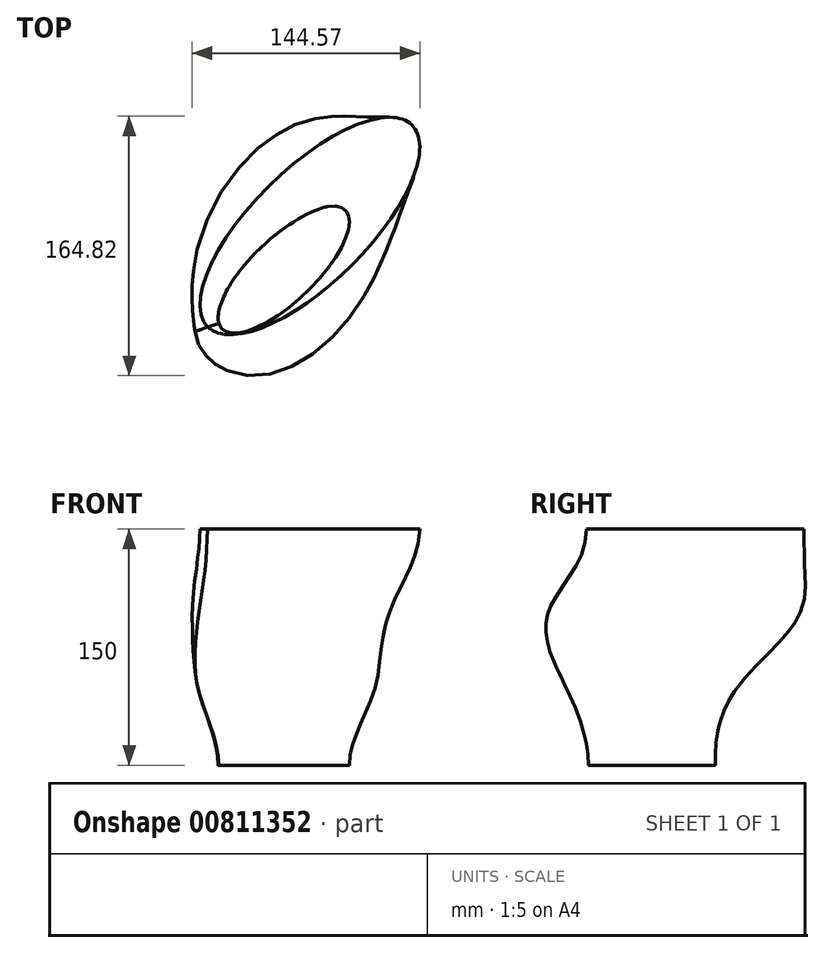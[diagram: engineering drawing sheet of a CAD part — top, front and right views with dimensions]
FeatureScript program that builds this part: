
annotation { "Feature Type Name" : "Feature", "Feature Type Description" : "" }
export const myFeature = defineFeature(function(context is Context, id is Id, definition is map)
    precondition{}
    {
        {
            var Q0;
            Q0=qCreatedBy(makeId("Top.planeOp"),FACE);
            var sketch = newSketch(context, id + "F0", { "sketchPlane" : qUnion([Q0])});
            skEllipse(sketch, "E0", {"center": v(36.85, 27.7) * mm, "majorRadius": 91.27 * mm, "minorRadius": 36.4 * mm, "majorAxis": v(-0.71, -0.7)});
            skSolve(sketch);
        }
        {
            var Q0;
            Q0=qCreatedBy(makeId("Top.planeOp"),FACE);
            cPlane(context, id + "F1", {"entities" : qUnion([Q0]), "cplaneType" : CPlaneType.OFFSET, "offset" : 50 * mm, "oppositeDirection" : true, "width" : 150 * mm, "height" : 150 * mm});
        }
        {
            var Q0;
            Q0=qCreatedBy(id+"F1.planeOp",FACE);
            var sketch = newSketch(context, id + "F2", { "sketchPlane" : qUnion([Q0])});
            skEllipse(sketch, "E1", {"center": v(25.4, 15.4) * mm, "majorRadius": 85.47 * mm, "minorRadius": 55.7 * mm, "majorAxis": v(0.46, 0.89)});
            skSolve(sketch);
        }
        {
            var Q0;
            Q0=qCreatedBy(id+"F1.planeOp",FACE);
            cPlane(context, id + "F3", {"entities" : qUnion([Q0]), "cplaneType" : CPlaneType.OFFSET, "offset" : 50 * mm, "oppositeDirection" : true, "width" : 150 * mm, "height" : 150 * mm});
        }
        {
            var Q0;
            Q0=qCreatedBy(id+"F3.planeOp",FACE);
            var sketch = newSketch(context, id + "F4", { "sketchPlane" : qUnion([Q0])});
            skEllipse(sketch, "E2", {"center": v(22.04, 0) * mm, "majorRadius": 71.84 * mm, "minorRadius": 31.93 * mm, "majorAxis": v(-0.72, -0.69)});
            skSolve(sketch);
        }
        {
            var Q0;
            Q0=qCreatedBy(id+"F3.planeOp",FACE);
            cPlane(context, id + "F5", {"entities" : qUnion([Q0]), "cplaneType" : CPlaneType.OFFSET, "offset" : 50 * mm, "oppositeDirection" : true, "width" : 150 * mm, "height" : 150 * mm});
        }
        {
            var Q0;
            Q0=qCreatedBy(id+"F5.planeOp",FACE);
            var sketch = newSketch(context, id + "F6", { "sketchPlane" : qUnion([Q0])});
            skEllipse(sketch, "E3", {"center": v(20.29, 0) * mm, "majorRadius": 54.33 * mm, "minorRadius": 20.27 * mm, "majorAxis": v(0.72, 0.7)});
            skSolve(sketch);
        }
        {
            var Q0;
            Q0 = qSketchRegion(id + "F0", true);
            var Q1;
            Q1 = qSketchRegion(id + "F2", true);
            var Q2;
            Q2 = qSketchRegion(id + "F4", true);
            var Q3;
            Q3 = qSketchRegion(id + "F6", true);
            var Q4;
            Q4=sQuery(id+"F0.wireOp",EDGE,"E0");
            var Q5;
            Q5=sQuery(id+"F2.wireOp",EDGE,"E1");
            var Q6;
            Q6=sQuery(id+"F4.wireOp",EDGE,"E2");
            var Q7;
            Q7=sQuery(id+"F6.wireOp",EDGE,"E3");
            loft(context, id + "F7", {"bodyType" : ToolBodyType.SURFACE, "startCondition" : LoftEndDerivativeType.NORMAL_TO_PROFILE, "startMagnitude" : 1, "endCondition" : LoftEndDerivativeType.NORMAL_TO_PROFILE, "endMagnitude" : 1, "sheetProfilesArray" : [{ "sheetProfileEntities" : qUnion([Q0]) }, { "sheetProfileEntities" : qUnion([Q1]) }, { "sheetProfileEntities" : qUnion([Q2]) }, { "sheetProfileEntities" : qUnion([Q3]) }], "wireProfilesArray" : [{ "wireProfileEntities" : qUnion([Q4]) }, { "wireProfileEntities" : qUnion([Q5]) }, { "wireProfileEntities" : qUnion([Q6]) }, { "wireProfileEntities" : qUnion([Q7]) }]});
        }
    });
